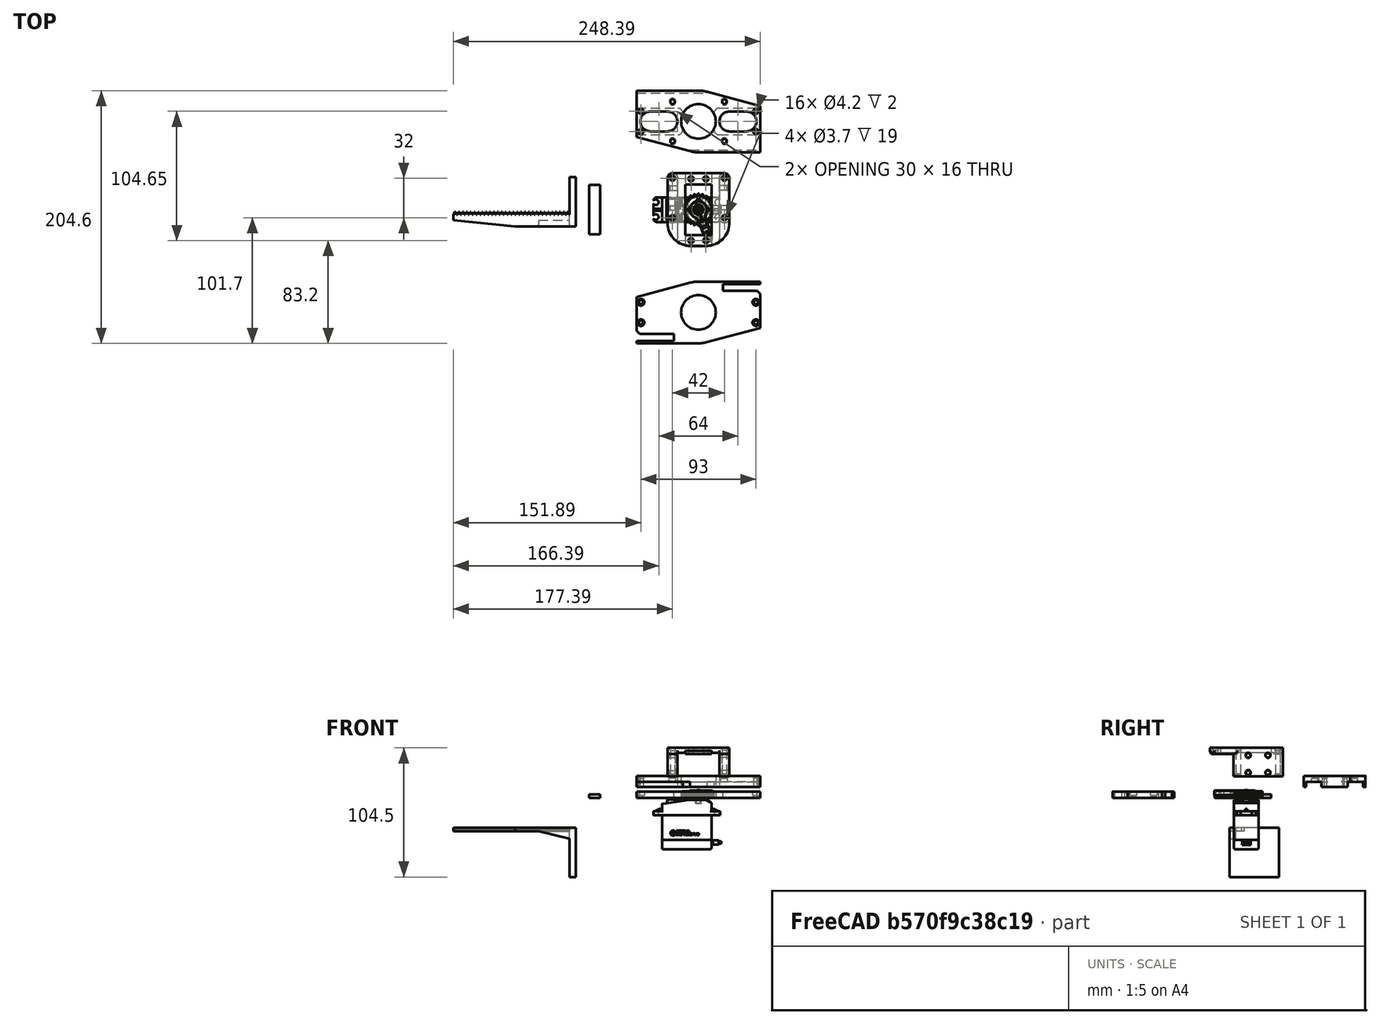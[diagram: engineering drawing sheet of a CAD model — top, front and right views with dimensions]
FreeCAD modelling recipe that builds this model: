
FCSTD DOCUMENT  (FreeCAD 1.1R20251125 (Git shallow))
Label: Pince_double_cremailleres
License: All rights reserved
LicenseURL: https://en.wikipedia.org/wiki/All_rights_reserved
objects: Sketcher::SketchObject×18, App::FeaturePython×13, PartDesign::Mirrored×11, App::Point×10, App::Link×9, PartDesign::Pad×7, PartDesign::Body×7, PartDesign::Pocket×6, PartDesign::Hole×6, PartDesign::Fillet×6, PartDesign::Chamfer×4, Part::FeaturePython×3, PartDesign::PolarPattern×3, PartDesign::MultiTransform×3, Part::Feature×3, PartDesign::FeatureBase×2, App::Part×2, PartDesign::Revolution×1, App::VarSet×1, Assembly::SimulationGroup×1, +2 more types
note: 177 computed .brp shape members not serialized (recipe doc carries the construction recipe); baked Part::Feature solids carry a one-line shape summary decoded from their .brp

FEATURE [Part::FeaturePython] InvoluteGear001  label="InvoluteGear_11_77"  # WARN: FeaturePython — macro-defined, semantics opaque (R4)
  AttacherType = Attacher::AttachEngine3D
  addendum_diameter = 26
  angular_backlash = 0
  axle_hole = false
  axle_holesize = 10
  backlash = 0
  clearance = 0.25
  double_helix = false
  head = 0
  head_fillet = 0
  height = 5.5
  helix_angle = 0
  module = 1
  num_teeth = 24
  numpoints = 20
  offset_hole = false
  offset_holeoffset = 10
  offset_holesize = 10
  pitch_diameter = 24
  pressure_angle = 20
  properties_from_tool = false
  reversed_backlash = false
  root_diameter = 21.5
  root_fillet = 0
  shift = 0
  simple = false
  transverse_pitch = 3.14159
  traverse_module = 1
  undercut = false
  version = 1.3.0
  expr: angular_backlash = backlash / pitch_diameter * 360 ° / pi
FEATURE [PartDesign::FeatureBase] BaseFeature003
  BaseFeature = -> InvoluteGear001
  Suppressed = false
FEATURE [Part::FeaturePython] InvoluteRack001  label="InvoluteRack_11_77"  # WARN: FeaturePython — macro-defined, semantics opaque (R4)
  AttacherType = Attacher::AttachEngine3D
  add_endings = true
  clearance = 0.25
  double_helix = false
  head = 0
  head_fillet = 0
  height = 3
  helix_angle = 0
  module = 1
  num_teeth = 30
  pressure_angle = 20
  properties_from_tool = false
  root_fillet = 0
  simplified = false
  thickness = 9.5
  transverse_pitch = 3.14159
  version = 1.3.0
FEATURE [PartDesign::FeatureBase] BaseFeature002
  BaseFeature = -> InvoluteRack001
  Suppressed = false
FEATURE [App::Point] Origin306  label="Origine"
  Role = Origin
FEATURE [App::Point] Origin311  label="Origine038"
  Role = Origin
FEATURE [App::Point] Origin312  label="Origine039"
  Role = Origin
FEATURE [App::Point] Origin314  label="Origine041"
  Role = Origin
FEATURE [Sketcher::SketchObject] Sketch244
  ArcFitTolerance = 1e-06
  AttachmentSupport = -> [BaseFeature002]
  ExternalTypes = [0]
  FullyConstrained = true
  MakeInternals = false
  MapMode = 5
  Placement = pos=(0,92.677,0) rot=(0,0.707107,0.707107;3.14159rad)
  sketch-geometry (4):
    g0: LineSegment StartX=-29.25 StartY=0 StartZ=0 EndX=10.75 EndY=0 EndZ=0
    g1: LineSegment StartX=10.75 StartY=0 StartZ=0 EndX=10.75 EndY=40 EndZ=0
    g2: LineSegment StartX=10.75 StartY=40 StartZ=0 EndX=-29.25 EndY=40 EndZ=0
    g3: LineSegment StartX=-29.25 StartY=40 StartZ=0 EndX=-29.25 EndY=0 EndZ=0
  constraints (12):
    c: Coincident(g0,g1)
    c: Coincident(g1,g2)
    c: Coincident(g2,g3)
    c: Coincident(g3,g0)
    c: Horizontal(g0)
    c: Horizontal(g2)
    c: Vertical(g1)
    c: Vertical(g3)
    c: DistanceY(g3,g3) = 40
    c: DistanceX(g2,g2) = 40
    c: PointOnObject(g0,g-1)
    c: DistanceX(g-1,g0) = 10.75
FEATURE [PartDesign::Pad] Pad119
  BaseFeature = -> BaseFeature002
  Direction = (0,1,-2e-16)
  Length = 5
  Length2 = 10
  Profile = -> Sketch244
  ReferenceAxis = -> Sketch244 [N_Axis]
  Refine = true
  SideType = 0
  Suppressed = false
  Type = 0
  Type2 = 0
FEATURE [Sketcher::SketchObject] Sketch253
  ArcFitTolerance = 0
  ExternalTypes = [0]
  FullyConstrained = true
  MakeInternals = false
  MapMode = 5
  Placement = pos=(0,0,5.5) rot=(0,0,1;0rad)
  sketch-geometry (8):
    g0: Circle [constr] CenterX=0 CenterY=0 CenterZ=0 NormalX=0 NormalY=0 NormalZ=1 AngleXU=0 Radius=7
    g1: Circle CenterX=0 CenterY=7 CenterZ=0 NormalX=0 NormalY=0 NormalZ=1 AngleXU=0 Radius=1.65
    g2: Circle CenterX=-7 CenterY=0 CenterZ=0 NormalX=0 NormalY=0 NormalZ=1 AngleXU=0 Radius=1.65
    g3: Circle CenterX=7 CenterY=0 CenterZ=0 NormalX=0 NormalY=0 NormalZ=1 AngleXU=0 Radius=1.65
    g4: Circle CenterX=0 CenterY=-7 CenterZ=0 NormalX=0 NormalY=0 NormalZ=1 AngleXU=0 Radius=1.65
    g5: Circle CenterX=0 CenterY=0 CenterZ=0 NormalX=0 NormalY=0 NormalZ=1 AngleXU=0 Radius=3
    g6: LineSegment [constr] StartX=-7 StartY=0 StartZ=0 EndX=7 EndY=0 EndZ=0
    g7: LineSegment [constr] StartX=0 StartY=7 StartZ=0 EndX=0 EndY=-7 EndZ=0
  constraints (20):
    c: Coincident(g5,g0)
    c: Coincident(g5,g-1)
    c: PointOnObject(g2,g0)
    c: PointOnObject(g1,g0)
    c: PointOnObject(g3,g0)
    c: PointOnObject(g4,g0)
    c: Coincident(g2,g6)
    c: Coincident(g1,g7)
    c: Coincident(g6,g3)
    c: Coincident(g7,g4)
    c: PointOnObject(g5,g7)
    c: PointOnObject(g5,g6)
    c: Perpendicular(g7,g6)
    c: Equal(g1,g3)
    c: Equal(g1,g2)
    c: Equal(g1,g4)
    c: Diameter(g1) = 3.3
    c: Diameter(g5) = 6
    c: Diameter(g0) = 14
    c: PointOnObject(g2,g-1)
FEATURE [PartDesign::Pocket] Pocket106
  BaseFeature = -> BaseFeature003
  Direction = (0,0,-1)
  Length = 5
  Length2 = 100
  Profile = -> Sketch253
  SideType = 0
  Suppressed = false
  Type = 1
  Type2 = 0
FEATURE [Sketcher::SketchObject] Sketch254
  ArcFitTolerance = 0
  AttachmentSupport = -> [Pocket106]
  ExternalGeometry = -> [Pocket106]
  ExternalTypes = [0]
  FullyConstrained = true
  MakeInternals = false
  MapMode = 5
  Placement = pos=(0,0,0) rot=(1,0,0;3.14159rad)
  sketch-geometry (4):
    g0: Circle CenterX=0 CenterY=-7 CenterZ=0 NormalX=0 NormalY=0 NormalZ=1 AngleXU=0 Radius=3.25
    g1: Circle CenterX=-7 CenterY=0 CenterZ=0 NormalX=0 NormalY=0 NormalZ=1 AngleXU=0 Radius=3.25
    g2: Circle CenterX=7 CenterY=0 CenterZ=0 NormalX=0 NormalY=0 NormalZ=1 AngleXU=0 Radius=3.25
    g3: Circle CenterX=0 CenterY=7 CenterZ=0 NormalX=0 NormalY=0 NormalZ=1 AngleXU=0 Radius=3.25
  constraints (8):
    c: Coincident(g1,g-5)
    c: Coincident(g0,g-3)
    c: Coincident(g2,g-4)
    c: Coincident(g3,g-6)
    c: Equal(g2,g0)
    c: Equal(g2,g1)
    c: Equal(g2,g3)
    c: Diameter(g2) = 6.5
FEATURE [PartDesign::Pocket] Pocket107
  BaseFeature = -> Pocket106
  Direction = (0,0,1)
  Length = 3.5
  Length2 = 100
  Profile = -> Sketch254
  SideType = 0
  Suppressed = false
  Type = 0
  Type2 = 0
FEATURE [PartDesign::Body] Body086  label="pignon"
  AllowCompound = false
  BaseFeature = -> InvoluteGear001
  Group = -> [BaseFeature003,Sketch253,Pocket106,Sketch254,Pocket107]
  Origin = -> Origin287
  Placement = pos=(-4.5e-15,0,0) rot=(0,0,1;0rad)
  Tip = -> Pocket107
FEATURE [Sketcher::SketchObject] Sketch259
  ArcFitTolerance = 1e-06
  AttachmentSupport = -> [XZ_Plane286]
  ExternalTypes = [0]
  FullyConstrained = true
  MakeInternals = false
  MapMode = 5
  Placement = pos=(0,0,0) rot=(1,0,0;1.5708rad)
  sketch-geometry (4):
    g0: LineSegment StartX=-4.5 StartY=0 StartZ=0 EndX=4.5 EndY=0 EndZ=0
    g1: LineSegment StartX=4.5 StartY=0 StartZ=0 EndX=4.5 EndY=3 EndZ=0
    g2: LineSegment StartX=4.5 StartY=3 StartZ=0 EndX=-4.5 EndY=3 EndZ=0
    g3: LineSegment StartX=-4.5 StartY=3 StartZ=0 EndX=-4.5 EndY=0 EndZ=0
  constraints (11):
    c: Coincident(g0,g1)
    c: Coincident(g1,g2)
    c: Coincident(g2,g3)
    c: Coincident(g3,g0)
    c: Horizontal(g0)
    c: Vertical(g1)
    c: Vertical(g3)
    c: PointOnObject(g0,g-1)
    c: Symmetric(g1,g2,g-2)
    c: Distance(g2,g2) = 9
    c: DistanceY(g3,g3) = 3
FEATURE [PartDesign::Pad] Pad123
  Direction = (0,-1,2e-16)
  Length = 40
  Length2 = 10
  Placement = pos=(0,0,0) rot=(1,0,0;1.5708rad)
  Profile = -> Sketch259
  ReferenceAxis = -> Sketch259 [N_Axis]
  SideType = 2
  Suppressed = false
  Type = 0
  Type2 = 0
FEATURE [PartDesign::Body] Body088  label="mousse"
  AllowCompound = false
  Group = -> [Sketch259,Pad123]
  Origin = -> Origin289
  Placement = pos=(-84,0,0) rot=(0,0,1;0rad)
  Tip = -> Pad123
FEATURE [Sketcher::SketchObject] Sketch262
  ArcFitTolerance = 1e-06
  AttachmentOffset = pos=(0,0,-10.75) rot=(0,0,1;0rad)
  AttachmentSupport = -> [YZ_Plane282]
  ExternalGeometry = -> [Pad119]
  ExternalTypes = [0]
  FullyConstrained = true
  MakeInternals = false
  MapMode = 5
  Placement = pos=(-10.75,0,0) rot=(0.57735,0.57735,0.57735;2.0944rad)
  sketch-geometry (3):
    g0: LineSegment StartX=67.677 StartY=3 StartZ=0 EndX=92.677 EndY=9 EndZ=0
    g1: LineSegment StartX=67.677 StartY=3 StartZ=0 EndX=92.677 EndY=3 EndZ=0
    g2: LineSegment StartX=92.677 StartY=9 StartZ=0 EndX=92.677 EndY=3 EndZ=0
  constraints (8):
    c: PointOnObject(g0,g-4)
    c: Coincident(g1,g0)
    c: Coincident(g1,g-4)
    c: Coincident(g2,g0)
    c: Coincident(g2,g1)
    c: DistanceX(g1,g1) = 25
    c: Vertical(g2)
    c: DistanceY(g2,g2) = 6
FEATURE [PartDesign::Pad] Pad124
  BaseFeature = -> Pad119
  Direction = (1,0,0)
  Length = 5
  Length2 = 10
  Profile = -> Sketch262
  ReferenceAxis = -> Sketch262 [N_Axis]
  SideType = 0
  Suppressed = false
  Type = 0
  Type2 = 0
FEATURE [App::Point] Origin317  label="Origine044"
  Role = Origin
FEATURE [Sketcher::SketchObject] Sketch
  ArcFitTolerance = 1e-06
  AttachmentSupport = -> [Origin]
  ExternalTypes = [0]
  FullyConstrained = true
  MakeInternals = false
  MapMode = 5
  expr: Constraints[23] = 28 / 2
  expr: Constraints[28] = 16.5 / 2
  sketch-geometry (17):
    g0: LineSegment StartX=-50 StartY=0 StartZ=0 EndX=-14 EndY=0 EndZ=0
    g1: LineSegment StartX=50 StartY=0 StartZ=0 EndX=50 EndY=15 EndZ=0
    g2: LineSegment [constr] StartX=1.5e-15 StartY=25 StartZ=0 EndX=-50 EndY=25 EndZ=0
    g3: LineSegment [constr] StartX=-50 StartY=25 StartZ=0 EndX=-50 EndY=12.5 EndZ=0
    g4: ArcOfCircle CenterX=0 CenterY=0 CenterZ=0 NormalX=0 NormalY=0 NormalZ=1 AngleXU=0 Radius=14 StartAngle=0 EndAngle=3.14159
    g5: LineSegment StartX=14 StartY=0 StartZ=0 EndX=50 EndY=0 EndZ=0
    g6: Circle CenterX=-46.5 CenterY=8.25 CenterZ=0 NormalX=0 NormalY=0 NormalZ=1 AngleXU=0 Radius=1.65
    g7: LineSegment StartX=50 StartY=23 StartZ=0 EndX=20 EndY=23 EndZ=0
    g8: LineSegment StartX=20 StartY=23 StartZ=0 EndX=20 EndY=17.5 EndZ=0
    g9: LineSegment StartX=20 StartY=17.5 StartZ=0 EndX=47.5 EndY=17.5 EndZ=0
    g10: LineSegment StartX=50 StartY=23 StartZ=0 EndX=50 EndY=25 EndZ=0
    g11: LineSegment StartX=47.5 StartY=17.5 StartZ=0 EndX=50 EndY=15 EndZ=0
    g12: Circle CenterX=46.5 CenterY=8.25 CenterZ=0 NormalX=0 NormalY=0 NormalZ=1 AngleXU=0 Radius=1.65
    g13: ArcOfCircle CenterX=0 CenterY=0 CenterZ=0 NormalX=0 NormalY=0 NormalZ=1 AngleXU=0 Radius=25 StartAngle=1.5708 EndAngle=1.83226
    g14: LineSegment StartX=-6.46242 StartY=24.1503 StartZ=0 EndX=-50 EndY=12.5 EndZ=0
    g15: LineSegment StartX=1.5e-15 StartY=25 StartZ=0 EndX=50 EndY=25 EndZ=0
    g16: LineSegment StartX=-50 StartY=12.5 StartZ=0 EndX=-50 EndY=0 EndZ=0
  constraints (47):
    c: Coincident(g5,g1)
    c: Coincident(g2,g3)
    c: PointOnObject(g0,g-1)
    c: Symmetric(g10,g2,g-2)
    c: Coincident(g4,g-1)
    c: Horizontal(g0)
    c: Horizontal(g5)
    c: Coincident(g4,g0)
    c: Coincident(g4,g5)
    c: Coincident(g7,g8)
    c: Coincident(g8,g9)
    c: Horizontal(g7)
    c: Vertical(g8)
    c: Vertical(g10)
    c: Coincident(g7,g10)
    c: Horizontal(g9)
    c: Coincident(g11,g9)
    c: Vertical(g1)
    c: Coincident(g11,g1)
    c: Vertical(g7,g1)
    c: Symmetric(g12,g6,g-2)
    c: Equal(g6,g12)
    c: DistanceX(g0,g6) = 3.5
    c: Radius(g4) = 14
    c: Angle(g11,g1) = 2.35619
    c: PointOnObject(g4,g-1)
    c: DistanceX(g7,g7) = 30
    c: DistanceY(g8,g8) = 5.5
    c: DistanceY(g1,g12) = 8.25
    c: DistanceY(g10,g10) = 2
    c: DistanceY(g1,g9) = 2.5
    c: Diameter(g12) = 3.3
    c: Coincident(g13,g4)
    c: Tangent(g14,g13) = -1.5708
    c: Coincident(g15,g13)
    c: Coincident(g16,g14)
    c: Coincident(g2,g13)
    c: DistanceX(g14,g10) = 100
    c: Coincident(g15,g10)
    c: Vertical(g3)
    c: Coincident(g3,g14)
    c: Coincident(g16,g0)
    c: DistanceY(g-1,g2) = 25
    c: Equal(g16,g3)
    c: Horizontal(g2)
    c: PointOnObject(g2,g-2)
    c: Vertical(g16)
FEATURE [PartDesign::Pad] Pad
  Direction = (0,0,1)
  Length = 5
  Length2 = 10
  Profile = -> Sketch
  ReferenceAxis = -> Sketch [N_Axis]
  SideType = 0
  Suppressed = false
  Type = 0
  Type2 = 0
FEATURE [PartDesign::Hole] Hole
  BaseFeature = -> Pad
  BaseProfileType = 7
  CustomThreadClearance = 0
  Depth = 3
  DepthType = 0
  Diameter = 5.5
  DrillForDepth = false
  DrillPoint = 0
  DrillPointAngle = 118
  HoleCutCountersinkAngle = 90
  HoleCutCustomValues = false
  HoleCutDepth = 0
  HoleCutDiameter = 0
  HoleCutType = 0
  ModelThread = false
  Profile = -> Pad [Edge45,Edge42]
  Suppressed = false
  Tapered = false
  TaperedAngle = 90
  ThreadClass = 0
  ThreadDepth = 3
  ThreadDepthType = 0
  ThreadDiameter = 5.5
  ThreadDirection = 0
  ThreadFit = 0
  ThreadSize = 0
  ThreadType = 0
  Threaded = false
  UseCustomThreadClearance = false
  expr: Depth = VarSet.h_tete_vis
  expr: Diameter = VarSet.d_tete_vis
FEATURE [PartDesign::PolarPattern] PolarPattern
  Angle = 360
  Axis = -> Sketch [N_Axis]
  BaseFeature = -> Hole
  Mode = 0
  Occurrences = 2
  Offset = 120
  Originals = -> [Pad,Hole]
  Refine = true
  SpacingPattern = [0]
  Spacings = [-1]
  Suppressed = false
  TransformMode = 0
FEATURE [PartDesign::Body] Body  label="capot"
  AllowCompound = false
  Group = -> [Sketch,Pad,Hole,PolarPattern]
  Origin = -> Origin
  Placement = pos=(0,-83.2,0) rot=(0,0,1;0rad)
  Tip = -> PolarPattern
FEATURE [App::Point] Origin319  label="Origine046"
  Role = Origin
FEATURE [Sketcher::SketchObject] Sketch263
  ArcFitTolerance = 0
  AttachmentOffset = pos=(0,0,-2) rot=(0,0,1;0rad)
  AttachmentSupport = -> [XY_Plane289]
  ExternalTypes = [0]
  FullyConstrained = true
  MakeInternals = false
  MapMode = 2
  Placement = pos=(0,0,-2) rot=(0,0,1;0rad)
  expr: Constraints[10] = 41 / 2
  expr: Constraints[13] = 59 / 2
  sketch-geometry (8):
    g0: LineSegment StartX=-10.5 StartY=20.5 StartZ=0 EndX=10.5 EndY=20.5 EndZ=0
    g1: LineSegment StartX=10.5 StartY=20.5 StartZ=0 EndX=10.5 EndY=0 EndZ=0
    g2: LineSegment StartX=-10.5 StartY=0 StartZ=0 EndX=-10.5 EndY=20.5 EndZ=0
    g3: LineSegment StartX=-25 StartY=29.5 StartZ=0 EndX=25 EndY=29.5 EndZ=0
    g4: LineSegment StartX=25 StartY=29.5 StartZ=0 EndX=25 EndY=0 EndZ=0
    g5: LineSegment StartX=25 StartY=0 StartZ=0 EndX=10.5 EndY=0 EndZ=0
    g6: LineSegment StartX=-25 StartY=0 StartZ=0 EndX=-25 EndY=29.5 EndZ=0
    g7: LineSegment StartX=-10.5 StartY=0 StartZ=0 EndX=-25 EndY=0 EndZ=0
  constraints (22):
    c: Coincident(g0,g1)
    c: Coincident(g2,g0)
    c: Horizontal(g0)
    c: Vertical(g1)
    c: Vertical(g2)
    c: Coincident(g3,g4)
    c: Coincident(g4,g5)
    c: Coincident(g6,g3)
    c: Vertical(g4)
    c: DistanceX(g2,g1) = 21
    c: DistanceY(g2,g2) = 20.5
    c: DistanceX(g7,g2) = 14.5
    c: Vertical(g6)
    c: DistanceY(g4,g4) = 29.5
    c: Coincident(g7,g6)
    c: Horizontal(g3)
    c: Symmetric(g1,g2,g-1)
    c: Symmetric(g4,g7,g-1)
    c: Horizontal(g5)
    c: Coincident(g5,g1)
    c: Coincident(g7,g2)
    c: PointOnObject(g2,g-1)
FEATURE [PartDesign::Pad] Pad125
  AlongSketchNormal = false
  Direction = (0,0,1)
  Length = 5
  Length2 = 100
  Profile = -> Sketch263
  ReferenceAxis = -> Sketch263 [N_Axis]
  SideType = 0
  Suppressed = false
  Type = 0
  Type2 = 0
FEATURE [PartDesign::Mirrored] Mirrored
  BaseFeature = -> Pad125
  MirrorPlane = -> Sketch263 [H_Axis]
  Originals = -> [Pad125]
  Refine = true
  Suppressed = false
  TransformMode = 0
FEATURE [Sketcher::SketchObject] Sketch271
  ArcFitTolerance = 1e-06
  AttachmentSupport = -> [Mirrored]
  ExternalGeometry = -> [Mirrored]
  ExternalTypes = [0]
  FullyConstrained = true
  MakeInternals = false
  MapMode = 5
  Placement = pos=(0,0,-2) rot=(1,0,0;3.14159rad)
  sketch-geometry (4):
    g0: LineSegment StartX=25 StartY=-29.5 StartZ=0 EndX=25 EndY=10.5 EndZ=0
    g1: LineSegment StartX=25 StartY=10.5 StartZ=0 EndX=17 EndY=10.5 EndZ=0
    g2: LineSegment StartX=17 StartY=10.5 StartZ=0 EndX=17 EndY=-29.5 EndZ=0
    g3: LineSegment StartX=17 StartY=-29.5 StartZ=0 EndX=25 EndY=-29.5 EndZ=0
  constraints (11):
    c: Coincident(g0,g1)
    c: Coincident(g1,g2)
    c: Coincident(g2,g3)
    c: Coincident(g3,g0)
    c: Vertical(g0)
    c: Vertical(g2)
    c: Horizontal(g1)
    c: Horizontal(g3)
    c: Distance(g0,g2) = 8
    c: Distance(g1,g3) = 40
    c: Coincident(g0,g-3)
FEATURE [PartDesign::Pad] Pad127
  BaseFeature = -> Mirrored
  Direction = (0,0,-1)
  Length = 18
  Length2 = 10
  Profile = -> Sketch271
  ReferenceAxis = -> Sketch271 [N_Axis]
  SideType = 0
  Suppressed = false
  Type = 0
  Type2 = 0
FEATURE [Sketcher::SketchObject] Sketch272
  ArcFitTolerance = 1e-06
  AttachmentSupport = -> [Pad127]
  ExternalGeometry = -> [Pad127]
  ExternalTypes = [0,0]
  FullyConstrained = true
  MakeInternals = false
  MapMode = 5
  Placement = pos=(0,0,3) rot=(0,0,1;0rad)
  sketch-geometry (6):
    g0: GeomPoint X=21 Y=25.5 Z=0
    g1: GeomPoint X=21 Y=-6.5 Z=0
    g2: LineSegment [constr] StartX=0 StartY=9.5 StartZ=0 EndX=25 EndY=9.5 EndZ=0
    g3: LineSegment [constr] StartX=21 StartY=29.5 StartZ=0 EndX=21 EndY=9.5 EndZ=0
    g4: GeomPoint X=6 Y=25 Z=0
    g5: GeomPoint X=6 Y=-25 Z=0
  constraints (12):
    c: PointOnObject(g2,g-2)
    c: Horizontal(g2)
    c: Symmetric(g-3,g-3,g2)
    c: Symmetric(g0,g1,g2)
    c: Symmetric(g-4,g-4,g3)
    c: PointOnObject(g3,g2)
    c: Vertical(g3)
    c: PointOnObject(g0,g3)
    c: DistanceY(g3,g0) = 16
    c: Distance(g4,g-2) = 6
    c: Symmetric(g4,g5,g-1)
    c: DistanceY(g-1,g4) = 25
FEATURE [PartDesign::Hole] Hole001
  BaseFeature = -> Pad127
  BaseProfileType = 1
  CustomThreadClearance = 0
  Depth = 26
  DepthType = 0
  Diameter = 3.7
  DrillForDepth = false
  DrillPoint = 0
  DrillPointAngle = 118
  HoleCutCountersinkAngle = 90
  HoleCutCustomValues = false
  HoleCutDepth = 2
  HoleCutDiameter = 4.2
  HoleCutType = 1
  ModelThread = false
  Profile = -> Sketch272
  Suppressed = false
  Tapered = false
  TaperedAngle = 90
  ThreadClass = 0
  ThreadDepth = 26
  ThreadDepthType = 0
  ThreadDiameter = 3.7
  ThreadDirection = 0
  ThreadFit = 0
  ThreadSize = 0
  ThreadType = 0
  Threaded = false
  UseCustomThreadClearance = false
  expr: Diameter = VarSet.d1_insert
  expr: HoleCutDepth = VarSet.h_d2_insert
  expr: HoleCutDiameter = VarSet.d2_insert
FEATURE [Sketcher::SketchObject] Sketch267
  ArcFitTolerance = 1e-06
  AttachmentSupport = -> [Hole001]
  ExternalGeometry = -> [Hole001]
  ExternalTypes = [0,0]
  FullyConstrained = true
  MakeInternals = false
  MapMode = 5
  Placement = pos=(25,0,0) rot=(0.57735,0.57735,0.57735;2.0944rad)
  sketch-geometry (6):
    g0: Circle CenterX=1.5 CenterY=-3 CenterZ=0 NormalX=0 NormalY=0 NormalZ=1 AngleXU=0 Radius=2.125
    g1: Circle CenterX=17.5 CenterY=-3 CenterZ=0 NormalX=0 NormalY=0 NormalZ=1 AngleXU=0 Radius=2.125
    g2: Circle CenterX=17.5 CenterY=-17 CenterZ=0 NormalX=0 NormalY=0 NormalZ=1 AngleXU=0 Radius=2.125
    g3: Circle CenterX=1.5 CenterY=-17 CenterZ=0 NormalX=0 NormalY=0 NormalZ=1 AngleXU=0 Radius=2.125
    g4: LineSegment [constr] StartX=9.5 StartY=-20 StartZ=0 EndX=9.5 EndY=0 EndZ=0
    g5: GeomPoint [constr] X=9.5 Y=-10 Z=0
  constraints (15):
    c: Equal(g0,g1)
    c: Equal(g1,g3)
    c: Equal(g3,g2)
    c: Diameter(g0) = 4.25
    c: Symmetric(g-3,g-3,g4)
    c: Vertical(g4)
    c: DistanceX(g0,g1) = 16
    c: DistanceY(g2,g1) = 14
    c: Vertical(g0,g3)
    c: Vertical(g2,g1)
    c: Horizontal(g1,g0)
    c: Horizontal(g2,g3)
    c: Symmetric(g4,g4,g5)
    c: Symmetric(g1,g3,g5)
    c: DistanceY(g-3,g3) = 3
FEATURE [PartDesign::Hole] Hole002
  BaseFeature = -> Hole001
  BaseProfileType = 7
  CustomThreadClearance = 0
  Depth = 25
  DepthType = 0
  Diameter = 3.7
  DrillForDepth = false
  DrillPoint = 0
  DrillPointAngle = 118
  HoleCutCountersinkAngle = 90
  HoleCutCustomValues = false
  HoleCutDepth = 2
  HoleCutDiameter = 4.2
  HoleCutType = 1
  ModelThread = false
  Profile = -> Sketch267
  Suppressed = false
  Tapered = false
  TaperedAngle = 90
  ThreadClass = 0
  ThreadDepth = 25
  ThreadDepthType = 0
  ThreadDiameter = 3.7
  ThreadDirection = 0
  ThreadFit = 0
  ThreadSize = 0
  ThreadType = 0
  Threaded = false
  UseCustomThreadClearance = false
  expr: Diameter = VarSet.d1_insert
  expr: HoleCutDepth = VarSet.h_d2_insert
  expr: HoleCutDiameter = VarSet.d2_insert
FEATURE [PartDesign::Mirrored] Mirrored001
  BaseFeature = -> Hole002
  MirrorPlane = -> Sketch271 [V_Axis]
  Originals = -> [Pad127,Hole001,Hole002]
  Suppressed = false
  TransformMode = 0
FEATURE [App::Point] Origin321  label="Origine047"
  Role = Origin
FEATURE [Sketcher::SketchObject] Sketch273
  ArcFitTolerance = 1e-06
  AttachmentSupport = -> [Origin320]
  ExternalTypes = [0]
  FullyConstrained = true
  MakeInternals = false
  MapMode = 5
  expr: Constraints[25] = 28 / 2
  sketch-geometry (9):
    g0: LineSegment StartX=14 StartY=1e-15 StartZ=0 EndX=17 EndY=1e-15 EndZ=0
    g1: LineSegment StartX=50 StartY=1e-15 StartZ=0 EndX=50 EndY=25 EndZ=0
    g2: LineSegment StartX=50 StartY=25 StartZ=0 EndX=0 EndY=25 EndZ=0
    g3: LineSegment StartX=9e-16 StartY=25 StartZ=0 EndX=9e-16 EndY=14 EndZ=0
    g4: ArcOfCircle CenterX=0 CenterY=0 CenterZ=0 NormalX=0 NormalY=0 NormalZ=1 AngleXU=0 Radius=14 StartAngle=0 EndAngle=1.5708
    g5: ArcOfCircle CenterX=25 CenterY=1e-15 CenterZ=0 NormalX=0 NormalY=0 NormalZ=1 AngleXU=0 Radius=8 StartAngle=1.5708 EndAngle=3.14159
    g6: ArcOfCircle CenterX=39 CenterY=3.1e-15 CenterZ=0 NormalX=0 NormalY=0 NormalZ=1 AngleXU=0 Radius=8 StartAngle=0 EndAngle=1.5708
    g7: LineSegment StartX=25 StartY=8 StartZ=0 EndX=39 EndY=8 EndZ=0
    g8: LineSegment StartX=47 StartY=1e-15 StartZ=0 EndX=50 EndY=1e-15 EndZ=0
  constraints (27):
    c: Coincident(g8,g1)
    c: Coincident(g1,g2)
    c: Coincident(g2,g3)
    c: Horizontal(g2)
    c: Vertical(g1)
    c: Coincident(g4,g0)
    c: Vertical(g3)
    c: Coincident(g4,g3)
    c: Tangent(g5,g7) = 1.5708
    c: Tangent(g6,g7) = 1.5708
    c: Equal(g5,g6)
    c: Horizontal(g7)
    c: Horizontal(g0)
    c: Horizontal(g8)
    c: Coincident(g6,g8)
    c: Coincident(g0,g5)
    c: Horizontal(g0,g6)
    c: PointOnObject(g0,g-1)
    c: Horizontal(g5,g0)
    c: Coincident(g4,g-1)
    c: PointOnObject(g3,g-2)
    c: DistanceX(g2,g2) = 50
    c: DistanceY(g1,g1) = 25
    c: Radius(g6) = 8
    c: DistanceX(g6,g1) = 11
    c: Radius(g4) = 14
    c: Equal(g8,g0)
FEATURE [PartDesign::Pad] Pad128
  Direction = (0,0,1)
  Length = 9
  Length2 = 10
  Profile = -> Sketch273
  ReferenceAxis = -> Sketch273 [N_Axis]
  SideType = 0
  Suppressed = false
  Type = 0
  Type2 = 0
FEATURE [PartDesign::Mirrored] Mirror
  MirrorPlane = -> XZ_Plane290
  Suppressed = false
  TransformMode = 0
FEATURE [PartDesign::Mirrored] Mirror001
  MirrorPlane = -> YZ_Plane290
  Suppressed = false
  TransformMode = 0
FEATURE [PartDesign::MultiTransform] MultiTransform
  BaseFeature = -> Pad128
  Refine = true
  Suppressed = false
  TransformMode = 1
  Transformations = -> [Mirror,Mirror001]
FEATURE [Sketcher::SketchObject] Sketch274
  ArcFitTolerance = 1e-06
  AttachmentSupport = -> [MultiTransform]
  ExternalGeometry = -> [MultiTransform]
  ExternalTypes = [0]
  FullyConstrained = true
  MakeInternals = false
  MapMode = 5
  Placement = pos=(-50,1.4e-14,0) rot=(0.57735,-0.57735,-0.57735;2.0944rad)
  sketch-geometry (4):
    g0: LineSegment StartX=-23 StartY=0 StartZ=0 EndX=-10.75 EndY=0 EndZ=0
    g1: LineSegment StartX=-10.75 StartY=0 StartZ=0 EndX=-10.75 EndY=4 EndZ=0
    g2: LineSegment StartX=-10.75 StartY=4 StartZ=0 EndX=-23 EndY=4 EndZ=0
    g3: LineSegment StartX=-23 StartY=4 StartZ=0 EndX=-23 EndY=0 EndZ=0
  constraints (12):
    c: Coincident(g0,g1)
    c: Coincident(g1,g2)
    c: Coincident(g2,g3)
    c: Coincident(g3,g0)
    c: Horizontal(g0)
    c: Horizontal(g2)
    c: Vertical(g1)
    c: Vertical(g3)
    c: Distance(g1,g3) = 12.25
    c: Distance(g0,g2) = 4
    c: PointOnObject(g0,g-1)
    c: DistanceX(g-3,g0) = 2
FEATURE [PartDesign::Pocket] Pocket
  BaseFeature = -> MultiTransform
  Direction = (1,0,0)
  Length = 5
  Length2 = 5
  Profile = -> Sketch274
  ReferenceAxis = -> Sketch274 [N_Axis]
  SideType = 0
  Suppressed = false
  Type = 1
  Type2 = 0
FEATURE [PartDesign::Mirrored] Mirrored002
  BaseFeature = -> Pocket
  MirrorPlane = -> Sketch274 [V_Axis]
  Originals = -> [Pocket]
  Suppressed = false
  TransformMode = 0
FEATURE [Sketcher::SketchObject] Sketch275
  ArcFitTolerance = 1e-06
  AttachmentSupport = -> [Mirrored002]
  ExternalTypes = [0]
  FullyConstrained = true
  MakeInternals = false
  MapMode = 5
  Placement = pos=(0,0,9) rot=(0,0,1;0rad)
  sketch-geometry (1):
    g0: GeomPoint X=46.5 Y=8.25 Z=0
  constraints (2):
    c: DistanceX(g-1,g0) = 46.5
    c: DistanceY(g-1,g0) = 8.25
FEATURE [PartDesign::Hole] Hole003
  BaseFeature = -> Mirrored002
  BaseProfileType = 7
  CustomThreadClearance = 0
  Depth = 25
  DepthType = 0
  Diameter = 3.7
  DrillForDepth = false
  DrillPoint = 0
  DrillPointAngle = 118
  HoleCutCountersinkAngle = 90
  HoleCutCustomValues = false
  HoleCutDepth = 2
  HoleCutDiameter = 4.2
  HoleCutType = 1
  ModelThread = false
  Profile = -> Sketch275
  Suppressed = false
  Tapered = false
  TaperedAngle = 90
  ThreadClass = 0
  ThreadDepth = 25
  ThreadDepthType = 0
  ThreadDiameter = 3.7
  ThreadDirection = 0
  ThreadFit = 0
  ThreadSize = 0
  ThreadType = 0
  Threaded = false
  UseCustomThreadClearance = false
  expr: Diameter = VarSet.d1_insert
  expr: HoleCutDepth = VarSet.h_d2_insert
  expr: HoleCutDiameter = VarSet.d2_insert
FEATURE [PartDesign::Mirrored] Mirror002
  MirrorPlane = -> Sketch275 [V_Axis]
  Suppressed = false
  TransformMode = 0
FEATURE [PartDesign::Mirrored] Mirror003
  MirrorPlane = -> Sketch275 [H_Axis]
  Suppressed = false
  TransformMode = 0
FEATURE [PartDesign::MultiTransform] MultiTransform001
  BaseFeature = -> Hole003
  Originals = -> [Hole003]
  Suppressed = false
  TransformMode = 0
  Transformations = -> [Mirror002,Mirror003]
FEATURE [Sketcher::SketchObject] Sketch276
  ArcFitTolerance = 1e-06
  AttachmentSupport = -> [MultiTransform001]
  ExternalTypes = [0]
  FullyConstrained = true
  MakeInternals = false
  MapMode = 5
  Placement = pos=(0,0,4) rot=(1,0,0;3.14159rad)
  expr: Constraints[0] = 32 / 2
  expr: Constraints[1] = 42 / 2
  sketch-geometry (1):
    g0: GeomPoint X=21 Y=16 Z=0
  constraints (2):
    c: DistanceY(g-1,g0) = 16
    c: DistanceX(g-1,g0) = 21
FEATURE [PartDesign::Hole] Hole004
  BaseFeature = -> MultiTransform001
  BaseProfileType = 7
  CustomThreadClearance = 0
  Depth = 10
  DepthType = 0
  Diameter = 3.7
  DrillForDepth = false
  DrillPoint = 0
  DrillPointAngle = 118
  HoleCutCountersinkAngle = 90
  HoleCutCustomValues = false
  HoleCutDepth = 3
  HoleCutDiameter = 5.5
  HoleCutType = 1
  ModelThread = false
  Profile = -> Sketch276
  Suppressed = false
  Tapered = false
  TaperedAngle = 90
  ThreadClass = 0
  ThreadDepth = 10
  ThreadDepthType = 0
  ThreadDiameter = 3.7
  ThreadDirection = 0
  ThreadFit = 0
  ThreadSize = 0
  ThreadType = 0
  Threaded = false
  UseCustomThreadClearance = false
  expr: Diameter = VarSet.d1_insert
  expr: HoleCutDepth = VarSet.h_tete_vis
  expr: HoleCutDiameter = VarSet.d_tete_vis
FEATURE [PartDesign::Mirrored] Mirror004
  MirrorPlane = -> Sketch276 [V_Axis]
  Suppressed = false
  TransformMode = 0
FEATURE [PartDesign::Mirrored] Mirror005
  MirrorPlane = -> Sketch276 [H_Axis]
  Suppressed = false
  TransformMode = 0
FEATURE [PartDesign::MultiTransform] MultiTransform002
  BaseFeature = -> Hole004
  Originals = -> [Hole004]
  Suppressed = false
  TransformMode = 0
  Transformations = -> [Mirror004,Mirror005]
FEATURE [PartDesign::Hole] Hole005
  BaseFeature = -> Mirrored001
  BaseProfileType = 7
  CustomThreadClearance = 0
  Depth = 2
  DepthType = 0
  Diameter = 4.2
  DrillForDepth = false
  DrillPoint = 0
  DrillPointAngle = 118
  HoleCutCountersinkAngle = 90
  HoleCutCustomValues = false
  HoleCutDepth = 0
  HoleCutDiameter = 0
  HoleCutType = 0
  ModelThread = false
  Profile = -> Mirrored001 [Edge143,Edge144]
  Reversed = true
  Suppressed = false
  Tapered = false
  TaperedAngle = 90
  ThreadClass = 0
  ThreadDepth = 2
  ThreadDepthType = 0
  ThreadDiameter = 4.2
  ThreadDirection = 0
  ThreadFit = 0
  ThreadSize = 0
  ThreadType = 0
  Threaded = false
  UseCustomThreadClearance = false
  expr: Depth = VarSet.h_d2_insert
  expr: Diameter = VarSet.d2_insert
FEATURE [PartDesign::Mirrored] Mirrored003
  BaseFeature = -> Hole005
  MirrorPlane = -> YZ_Plane289
  Originals = -> [Hole005]
  Suppressed = false
  TransformMode = 0
FEATURE [App::Point] Origin323  label="Origine049"
  Role = Origin
FEATURE [App::Link] cremaillere_bras  label="cremaillere_bras001"
  LinkPlacement = pos=(9.41322,21.75,-25) rot=(-0.707107,0.707107,0;3.14159rad)
  LinkedObject = -> Body084
  Placement = pos=(9.41322,21.75,-25) rot=(-0.707107,0.707107,0;3.14159rad)
FEATURE [App::Link] pignon  label="pignon001"
  LinkPlacement = pos=(8e-15,9.5,-26.2) rot=(0,0,-1;0.954906rad)
  LinkedObject = -> Body086
  Placement = pos=(8e-15,9.5,-26.2) rot=(0,0,-1;0.954906rad)
FEATURE [App::Link] mousse  label="mousse001"
  LinkPlacement = pos=(-83.2638,12.5,-60.5) rot=(0.707107,0,0.707107;3.14159rad)
  LinkedObject = -> Body088
  Placement = pos=(-83.2638,12.5,-60.5) rot=(0.707107,0,0.707107;3.14159rad)
FEATURE [App::Link] servo_DS3218MG003  label="servo_DS3218MG004"
  LinkPlacement = pos=(7.2e-15,9.5,-15.9) rot=(0.707107,0.707107,0;3.14159rad)
  LinkedObject = -> Part [Part002005.]
  Placement = pos=(7.2e-15,9.5,-15.9) rot=(0.707107,0.707107,0;3.14159rad)
FEATURE [App::Link] capot  label="capot001"
  LinkPlacement = pos=(-3.4e-15,9.5,-29) rot=(0,1,0;3.14159rad)
  LinkedObject = -> Body
  Placement = pos=(-3.4e-15,9.5,-29) rot=(0,1,0;3.14159rad)
FEATURE [App::Link] support_servo  label="support_servo001"
  LinkedObject = -> Body089
FEATURE [App::Link] support_cremaillere  label="support_cremaillere001"
  LinkPlacement = pos=(6e-15,9.5,-29) rot=(0,0,1;3.14159rad)
  LinkedObject = -> Body090
  Placement = pos=(6e-15,9.5,-29) rot=(0,0,1;3.14159rad)
FEATURE [App::Link] cremaillere_bras001  label="cremaillere_bras002"
  LinkPlacement = pos=(-9.43366,-2.75,-25) rot=(0.707107,0.707107,0;3.14159rad)
  LinkedObject = -> Body084
  Placement = pos=(-9.43366,-2.75,-25) rot=(0.707107,0.707107,0;3.14159rad)
FEATURE [App::Link] mousse001  label="mousse002"
  LinkPlacement = pos=(80.2433,6.5,-60.5) rot=(0,1,0;1.5708rad)
  LinkedObject = -> Body088
  Placement = pos=(80.2433,6.5,-60.5) rot=(0,1,0;1.5708rad)
FEATURE [App::FeaturePython] GroundedJoint  label="GroundedJoint002"  # Assembly grounded joint (typed FeaturePython)
  ObjectToGround = -> support_servo
FEATURE [App::Point] Origin326  label="Origine051"
  Role = Origin
FEATURE [App::Point] Origin327  label="Origine052"
  Role = Origin
FEATURE [Part::Feature] Part__Feature006  label="Lever 25T003"
  Placement = pos=(0,0,0) rot=(-1,0,0;1.5708rad)
  shape: bbox 18.84 x 33.03 x 6.019 mm, 125 faces (baked)
FEATURE [Part::Feature] Part__Feature007  label="Axis Servo003"
  Placement = pos=(0,0,0) rot=(-1,0,0;1.5708rad)
  shape: bbox 5 x 5 x 8 mm, 5 faces (baked)
FEATURE [Part::Feature] Part__Feature008  label="Servo DS3218MG003"
  Placement = pos=(0,0,0) rot=(-1,0,0;1.5708rad)
  shape: bbox 55 x 20 x 41 mm, 772 faces (baked)
FEATURE [Part::FeaturePython] Screw006  label="M2x5-Vis003"  # WARN: FeaturePython — macro-defined, semantics opaque (R4)
  BaseObject = -> Body091 [Edge6]
  Diameter = 2
  Invert = true
  LeftHanded = false
  Length = 10
  LengthCustom = 5
  MatchOuter = false
  OffsetAngle = 0
  Placement = pos=(0,1e-15,4.8) rot=(0,0,1;0rad)
  Thread = false
  Type = 76
FEATURE [Sketcher::SketchObject] Sketch277
  ArcFitTolerance = 0
  AttachmentSupport = -> [XZ_Plane293]
  ExternalTypes = [0]
  FullyConstrained = true
  MakeInternals = false
  MapMode = 5
  Placement = pos=(0,0,0) rot=(1,0,0;1.5708rad)
  expr: Constraints[19] = 19.8 / 2
  sketch-geometry (8):
    g0: LineSegment StartX=2.5 StartY=3.4 StartZ=0 EndX=2.5 EndY=0 EndZ=0
    g1: LineSegment StartX=2.5 StartY=0 StartZ=0 EndX=4.2 EndY=0 EndZ=0
    g2: LineSegment StartX=4.2 StartY=0 StartZ=0 EndX=4.2 EndY=2 EndZ=0
    g3: LineSegment StartX=4.2 StartY=2 StartZ=0 EndX=9.9 EndY=2 EndZ=0
    g4: LineSegment StartX=9.9 StartY=2 StartZ=0 EndX=9.9 EndY=4.4 EndZ=0
    g5: LineSegment StartX=9.9 StartY=4.4 StartZ=0 EndX=1.5 EndY=4.4 EndZ=0
    g6: LineSegment StartX=1.5 StartY=4.4 StartZ=0 EndX=1.5 EndY=3.4 EndZ=0
    g7: LineSegment StartX=1.5 StartY=3.4 StartZ=0 EndX=2.5 EndY=3.4 EndZ=0
  constraints (24):
    c: PointOnObject(g0,g-1)
    c: Vertical(g0)
    c: Coincident(g1,g0)
    c: PointOnObject(g1,g-1)
    c: Coincident(g2,g1)
    c: Vertical(g2)
    c: Coincident(g3,g2)
    c: Horizontal(g3)
    c: Coincident(g4,g3)
    c: Vertical(g4)
    c: Coincident(g5,g4)
    c: Horizontal(g5)
    c: Coincident(g6,g5)
    c: Coincident(g7,g6)
    c: Coincident(g7,g0)
    c: Horizontal(g7)
    c: Vertical(g6)
    c: DistanceY(g4,g4) = 2.4
    c: DistanceY(g2,g2) = 2
    c: DistanceX(g-1,g4) = 9.9
    c: DistanceX(g-1,g6) = 1.5
    c: DistanceY(g0,g0) = 3.4
    c: DistanceX(g-1,g0) = 2.5
    c: DistanceX(g1,g1) = 1.7
FEATURE [PartDesign::Revolution] Revolution003
  Angle = 360
  Angle2 = 60
  Axis = (0,2e-16,1)
  Base = (0,0,0)
  Placement = pos=(0,0,0) rot=(1,0,0;1.5708rad)
  Profile = -> Sketch277
  ReferenceAxis = -> Sketch277 [V_Axis]
  Reversed = true
  Suppressed = false
  Type = 0
FEATURE [Sketcher::SketchObject] Sketch278
  ArcFitTolerance = 0
  AttachmentSupport = -> [XY_Plane293]
  ExternalTypes = [0]
  FullyConstrained = true
  MakeInternals = false
  MapMode = 5
  sketch-geometry (1):
    g0: Circle CenterX=-7 CenterY=0 CenterZ=0 NormalX=0 NormalY=0 NormalZ=1 AngleXU=0 Radius=1.2
  constraints (3):
    c: PointOnObject(g0,g-1)
    c: Diameter(g0) = 2.4
    c: DistanceX(g0,g-1) = 7
FEATURE [PartDesign::Pocket] Pocket112
  BaseFeature = -> Revolution003
  Direction = (0,0,-1)
  Length = 5
  Length2 = 5
  Placement = pos=(0,0,0) rot=(1,0,0;1.5708rad)
  Profile = -> Sketch278
  ReferenceAxis = -> Sketch278 [N_Axis]
  SideType = 2
  Suppressed = false
  Type = 1
  Type2 = 0
FEATURE [PartDesign::PolarPattern] PolarPattern007
  Angle = 360
  Axis = -> Sketch278 [N_Axis]
  BaseFeature = -> Pocket112
  Mode = 0
  Occurrences = 4
  Offset = 120
  Originals = -> [Pocket112]
  Placement = pos=(0,0,0) rot=(1,0,0;1.5708rad)
  SpacingPattern = [0]
  Spacings = [-1,-1,-1]
  Suppressed = false
  TransformMode = 0
FEATURE [PartDesign::Body] Body091  label="Corps003"
  AllowCompound = false
  Group = -> [Sketch277,Revolution003,Sketch278,Pocket112,PolarPattern007]
  Origin = -> Origin325
  Placement = pos=(0,0,0.4) rot=(0,0,1;0rad)
  Tip = -> PolarPattern007
FEATURE [App::Part] Part002005  label="servo_DS3218MG005"
  Group = -> [Part__Feature006,Part__Feature007,Part__Feature008,Body091,Screw006]
  Origin = -> Origin324
FEATURE [App::FeaturePython] Joint010  label="Revolute016"  # Assembly joint (typed FeaturePython)
  Angle = 0
  AngleMax = 0
  AngleMin = 0
  Detach1 = false
  Detach2 = false
  Distance = 0
  Distance2 = 0
  EnableAngleMax = false
  EnableAngleMin = false
  EnableLengthMax = false
  EnableLengthMin = false
  JointType = 1 (Revolute)
  LengthMax = 0
  LengthMin = 0
  Placement1 = pos=(0,0,5.5) rot=(0,0,1;0rad)
  Reference1 = -> Assembly002 [pignon.Edge300,pignon.Edge300]
  Reference2 = -> Assembly002 [servo_DS3218MG003.Screw006.Edge63,servo_DS3218MG003.Screw006.Edge63]
  Suppressed = false
FEATURE [App::VarSet] VarSet
  d1_insert = 3.7
  d2_insert = 4.2
  d_tete_vis = 5.5
  h_d2_insert = 2
  h_tete_vis = 3
FEATURE [PartDesign::Fillet] Fillet
  Base = -> Mirrored003 [Edge67,Edge54]
  BaseFeature = -> Mirrored003
  Radius = 4
  SupportTransform = false
  Suppressed = false
  UseAllEdges = false
FEATURE [PartDesign::Fillet] Fillet001
  Base = -> Fillet [Edge3,Edge29]
  BaseFeature = -> Fillet
  Radius = 19
  SupportTransform = false
  Suppressed = false
  UseAllEdges = false
FEATURE [App::FeaturePython] Joint013  label="Fixed019"  # Assembly joint (typed FeaturePython)
  Angle = 0
  AngleMax = 0
  AngleMin = 0
  Detach1 = false
  Detach2 = false
  Distance = 0
  Distance2 = 0
  EnableAngleMax = false
  EnableAngleMin = false
  EnableLengthMax = false
  EnableLengthMin = false
  JointType = 0 (Fixed)
  LengthMax = 0
  LengthMin = 0
  Offset2 = pos=(0,0,0) rot=(0,0,1;3.14159rad)
  Placement1 = pos=(15.5,13.9,-6) rot=(0.57735,0.57735,0.57735;4.18879rad)
  Placement2 = pos=(-6,25,-2) rot=(1,0,0;3.14159rad)
  Reference1 = -> Assembly002 [servo_DS3218MG003.Part__Feature008.Edge1093,servo_DS3218MG003.Part__Feature008.Edge1093]
  Reference2 = -> Assembly002 [support_servo.Edge188,support_servo.Edge188]
  Suppressed = false
FEATURE [Sketcher::SketchObject] Sketch279
  ArcFitTolerance = 1e-06
  AttachmentSupport = -> [MultiTransform002]
  ExternalGeometry = -> [MultiTransform002]
  ExternalTypes = [0,0]
  FullyConstrained = true
  MakeInternals = false
  MapMode = 5
  Placement = pos=(0,0,4) rot=(1,0,0;3.14159rad)
  sketch-geometry (5):
    g0: LineSegment StartX=-50 StartY=12.5 StartZ=0 EndX=-6.46242 EndY=24.1503 EndZ=0
    g1: LineSegment StartX=1.5e-15 StartY=25 StartZ=0 EndX=-50 EndY=25 EndZ=0
    g2: LineSegment StartX=-50 StartY=25 StartZ=0 EndX=-50 EndY=12.5 EndZ=0
    g3: ArcOfCircle CenterX=0 CenterY=0 CenterZ=0 NormalX=0 NormalY=0 NormalZ=1 AngleXU=0 Radius=25 StartAngle=1.5708 EndAngle=1.83226
    g4: LineSegment [constr] StartX=-50 StartY=-1.21e-14 StartZ=0 EndX=-50 EndY=25 EndZ=0
  constraints (11):
    c: Horizontal(g1)
    c: Coincident(g2,g1)
    c: Coincident(g2,g0)
    c: Coincident(g3,g-1)
    c: Coincident(g3,g1)
    c: Tangent(g0,g3) = 1.5708
    c: Coincident(g1,g-4)
    c: Symmetric(g-3,g-3,g4)
    c: Coincident(g4,g1)
    c: Symmetric(g1,g4,g0)
    c: PointOnObject(g1,g-2)
FEATURE [PartDesign::Pocket] Pocket113
  BaseFeature = -> MultiTransform002
  Direction = (0,0,1)
  Length = 5
  Length2 = 5
  Profile = -> Sketch279
  ReferenceAxis = -> Sketch279 [N_Axis]
  SideType = 2
  Suppressed = false
  Type = 1
  Type2 = 0
FEATURE [PartDesign::PolarPattern] PolarPattern008
  Angle = 360
  Axis = -> Sketch279 [N_Axis]
  BaseFeature = -> Pocket113
  Mode = 0
  Occurrences = 2
  Offset = 120
  Originals = -> [Pocket113]
  SpacingPattern = [0]
  Spacings = [-1]
  Suppressed = false
  TransformMode = 0
FEATURE [PartDesign::Chamfer] Chamfer001
  Angle = 45
  Base = -> PolarPattern008 [Edge18,Edge133]
  BaseFeature = -> PolarPattern008
  ChamferType = 0
  FlipDirection = false
  Size = 4
  Size2 = 1
  SupportTransform = false
  Suppressed = false
  UseAllEdges = false
FEATURE [PartDesign::Fillet] Fillet004
  Base = -> Chamfer001 [Edge94,Edge89,Edge76,Edge95]
  BaseFeature = -> Chamfer001
  Radius = 4
  SupportTransform = false
  Suppressed = false
  UseAllEdges = false
FEATURE [PartDesign::Body] Body090  label="support_cremaillere"
  AllowCompound = false
  Group = -> [Sketch273,Pad128,MultiTransform,Mirror,Mirror001,Sketch274,Pocket,Mirrored002,Sketch275,Hole003,MultiTransform001,Mirror002,Mirror003,Sketch276,Hole004,MultiTransform002,Mirror004,Mirror005,Sketch279,Pocket113,PolarPattern008,Chamfer001,Fillet004]
  Origin = -> Origin320
  Placement = pos=(8.5e-15,71.4,8.9) rot=(0,0,1;0rad)
  Tip = -> Fillet004
FEATURE [PartDesign::Chamfer] Chamfer002
  Angle = 45
  Base = -> Pad124 [Edge2]
  BaseFeature = -> Pad124
  ChamferType = 1
  FlipDirection = false
  Size = 5
  Size2 = 50
  SupportTransform = false
  Suppressed = false
  UseAllEdges = false
FEATURE [PartDesign::Body] Body084  label="cremaillere_bras"
  AllowCompound = false
  BaseFeature = -> InvoluteRack001
  Group = -> [BaseFeature002,Sketch244,Pad119,Sketch262,Pad124,Chamfer002]
  Origin = -> Origin285
  Placement = pos=(-196.823,-2.75,-24) rot=(0.707107,0.707107,0;3.14159rad)
  Tip = -> Chamfer002
FEATURE [App::FeaturePython] Joint014  label="Slider025"  # Assembly joint (typed FeaturePython)
  Angle = 0
  AngleMax = 0
  AngleMin = 0
  Detach1 = false
  Detach2 = false
  Distance = 0
  Distance2 = 0
  EnableAngleMax = false
  EnableAngleMin = false
  EnableLengthMax = true
  EnableLengthMin = true
  JointType = 3 (Slider)
  LengthMax = -9
  LengthMin = -42
  Offset2 = pos=(0,0,0) rot=(0,0,1;3.14159rad)
  Placement1 = pos=(-10.75,73.0531,3.6e-15) rot=(0.57735,0.57735,0.57735;4.18879rad)
  Placement2 = pos=(-21.6194,23,4) rot=(0,-1,0;4.71239rad)
  Reference1 = -> Assembly002 [cremaillere_bras001.Edge7,cremaillere_bras001.Edge7]
  Reference2 = -> Assembly002 [support_cremaillere.Edge5,support_cremaillere.Edge5]
  Suppressed = false
FEATURE [App::FeaturePython] Joint015  label="Slider026"  # Assembly joint (typed FeaturePython)
  Angle = 0
  AngleMax = 0
  AngleMin = 0
  Detach1 = false
  Detach2 = false
  Distance = 0
  Distance2 = 0
  EnableAngleMax = false
  EnableAngleMin = false
  EnableLengthMax = false
  EnableLengthMin = false
  JointType = 3 (Slider)
  LengthMax = -9
  LengthMin = -42
  Offset2 = pos=(0,0,0) rot=(0,0,1;3.14159rad)
  Placement1 = pos=(-10.75,73.0531,7.1e-15) rot=(0.57735,0.57735,0.57735;4.18879rad)
  Placement2 = pos=(21.6194,-23,4) rot=(0,-1,0;4.71239rad)
  Reference1 = -> Assembly002 [cremaillere_bras.Edge7,cremaillere_bras.Edge7]
  Reference2 = -> Assembly002 [support_cremaillere.Edge112,support_cremaillere.Edge112]
  Suppressed = false
FEATURE [App::FeaturePython] Joint016  label="Fixed023"  # Assembly joint (typed FeaturePython)
  Angle = 0
  AngleMax = 0
  AngleMin = 0
  Detach1 = false
  Detach2 = false
  Distance = 0
  Distance2 = 0
  EnableAngleMax = false
  EnableAngleMin = false
  EnableLengthMax = false
  EnableLengthMin = false
  JointType = 0 (Fixed)
  LengthMax = 0
  LengthMin = 0
  Placement1 = pos=(-46.5,-8.25,0) rot=(0,0,1;3.14159rad)
  Placement2 = pos=(-46.5,8.25,-7.1e-15) rot=(0,-1,0;3.14159rad)
  Reference1 = -> Assembly002 [capot.Edge41,capot.Edge41]
  Reference2 = -> Assembly002 [support_cremaillere.Edge78,support_cremaillere.Edge78]
  Suppressed = false
FEATURE [App::FeaturePython] Joint017  label="Fixed024"  # Assembly joint (typed FeaturePython)
  Angle = 0
  AngleMax = 0
  AngleMin = 0
  Detach1 = false
  Detach2 = false
  Distance = 0
  Distance2 = 0
  EnableAngleMax = false
  EnableAngleMin = false
  EnableLengthMax = false
  EnableLengthMin = false
  JointType = 0 (Fixed)
  LengthMax = 0
  LengthMin = 0
  Offset2 = pos=(0,0,0) rot=(0,0,1;1.5708rad)
  Placement1 = pos=(4.5,2.7e-15,3) rot=(-0.57735,-0.57735,0.57735;4.18879rad)
  Placement2 = pos=(9.25,92.677,40) rot=(0.57735,-0.57735,0.57735;4.18879rad)
  Reference1 = -> Assembly002 [mousse001.Edge5,mousse001.Edge5]
  Reference2 = -> Assembly002 [cremaillere_bras001.Edge271,cremaillere_bras001.Edge271]
  Suppressed = false
FEATURE [App::FeaturePython] Joint018  label="Fixed025"  # Assembly joint (typed FeaturePython)
  Angle = 0
  AngleMax = 0
  AngleMin = 0
  Detach1 = false
  Detach2 = false
  Distance = 0
  Distance2 = 0
  EnableAngleMax = false
  EnableAngleMin = false
  EnableLengthMax = false
  EnableLengthMin = false
  JointType = 0 (Fixed)
  LengthMax = 0
  LengthMin = 0
  Offset2 = pos=(0,0,0) rot=(0,0,-1;1.5708rad)
  Placement1 = pos=(-4.5,-1.8e-15,0) rot=(-0.57735,-0.57735,0.57735;4.18879rad)
  Placement2 = pos=(9.25,92.677,40) rot=(0.57735,0.57735,0.57735;2.0944rad)
  Reference1 = -> Assembly002 [mousse.Edge1,mousse.Edge1]
  Reference2 = -> Assembly002 [cremaillere_bras.Edge271,cremaillere_bras.Edge271]
  Suppressed = false
FEATURE [App::FeaturePython] Joint019  label="RackPinion031"  # Assembly joint (typed FeaturePython)
  Angle = 0
  AngleMax = 0
  AngleMin = 0
  Detach1 = false
  Detach2 = false
  Distance = 12
  Distance2 = 0
  EnableAngleMax = false
  EnableAngleMin = false
  EnableLengthMax = false
  EnableLengthMin = false
  JointType = 9 (RackPinion)
  LengthMax = 0
  LengthMin = 0
  Placement1 = pos=(-10.75,58.0531,3) rot=(0.57735,0.57735,0.57735;4.18879rad)
  Reference1 = -> Assembly002 [cremaillere_bras001.Edge135,cremaillere_bras001.Edge135]
  Reference2 = -> Assembly002 [pignon.Edge154,pignon.Edge154]
  Suppressed = false
FEATURE [App::FeaturePython] Joint020  label="RackPinion032"  # Assembly joint (typed FeaturePython)
  Angle = 0
  AngleMax = 0
  AngleMin = 0
  Detach1 = false
  Detach2 = false
  Distance = 12
  Distance2 = 0
  EnableAngleMax = false
  EnableAngleMin = false
  EnableLengthMax = false
  EnableLengthMin = false
  JointType = 9 (RackPinion)
  LengthMax = 0
  LengthMin = 0
  Placement1 = pos=(-10.75,58.0531,3) rot=(0.57735,0.57735,0.57735;4.18879rad)
  Reference1 = -> Assembly002 [cremaillere_bras.Edge135,cremaillere_bras.Edge135]
  Reference2 = -> Assembly002 [pignon.Edge154,pignon.Edge154]
  Suppressed = false
FEATURE [App::FeaturePython] Motion  label="Slider025 (Linear)"  # WARN: FeaturePython — macro-defined, semantics opaque (R4)
  Formula = -9-25*time
  Joint = -> Joint014
  MotionType = 1
FEATURE [App::FeaturePython] Simulation  label="Simulation002"  # WARN: FeaturePython — macro-defined, semantics opaque (R4)
  Group = -> [Motion]
  aTimeStart = 0
  bTimeEnd = 1
  cTimeStepOutput = 0.01
  fGlobalErrorTolerance = 1e-06
  jFramesPerSecond = 30
FEATURE [Assembly::SimulationGroup] Simulations
  Group = -> [Simulation]
FEATURE [Sketcher::SketchObject] Sketch281
  ArcFitTolerance = 1e-06
  AttachmentSupport = -> [Fillet001]
  ExternalGeometry = -> [Fillet001]
  ExternalTypes = [0,0]
  FullyConstrained = true
  MakeInternals = false
  MapMode = 5
  Placement = pos=(0,29.5,0) rot=(0,0.707107,0.707107;3.14159rad)
  sketch-geometry (4):
    g0: LineSegment StartX=-17 StartY=-2 StartZ=0 EndX=-10.5 EndY=-2 EndZ=0
    g1: LineSegment StartX=-10.5 StartY=-2 StartZ=0 EndX=-10.5 EndY=-1 EndZ=0
    g2: LineSegment StartX=-10.5 StartY=-1 StartZ=0 EndX=-17 EndY=-1 EndZ=0
    g3: LineSegment StartX=-17 StartY=-1 StartZ=0 EndX=-17 EndY=-2 EndZ=0
  constraints (11):
    c: Coincident(g0,g1)
    c: Coincident(g1,g2)
    c: Coincident(g2,g3)
    c: Coincident(g3,g0)
    c: Horizontal(g0)
    c: Horizontal(g2)
    c: Vertical(g1)
    c: Vertical(g3)
    c: Coincident(g0,g-3)
    c: Vertical(g1,g-4)
    c: DistanceY(g1,g1) = 1
FEATURE [PartDesign::Pocket] Pocket114
  BaseFeature = -> Fillet001
  Direction = (0,-1,2e-16)
  Length = 5
  Length2 = 5
  Profile = -> Sketch281
  ReferenceAxis = -> Sketch281 [N_Axis]
  SideType = 0
  Suppressed = false
  Type = 1
  Type2 = 0
FEATURE [PartDesign::Mirrored] Mirrored004
  BaseFeature = -> Pocket114
  MirrorPlane = -> Sketch281 [V_Axis]
  Originals = -> [Pocket114]
  Suppressed = false
  TransformMode = 0
FEATURE [PartDesign::Fillet] Fillet002
  Base = -> Mirrored004 [Edge40,Edge193,Edge153,Edge123]
  BaseFeature = -> Mirrored004
  Radius = 3.5
  SupportTransform = false
  Suppressed = false
  UseAllEdges = false
FEATURE [PartDesign::Chamfer] Chamfer
  Angle = 45
  Base = -> Fillet002 [Edge71,Edge174]
  BaseFeature = -> Fillet002
  ChamferType = 0
  FlipDirection = false
  Size = 2
  Size2 = 1
  SupportTransform = false
  Suppressed = false
  UseAllEdges = false
FEATURE [PartDesign::Fillet] Fillet005
  Base = -> Chamfer [Edge132,Edge94]
  BaseFeature = -> Chamfer
  Radius = 2
  SupportTransform = false
  Suppressed = false
  UseAllEdges = false
FEATURE [PartDesign::Chamfer] Chamfer003
  Angle = 45
  Base = -> Fillet005 [Edge92]
  BaseFeature = -> Fillet005
  ChamferType = 1
  FlipDirection = false
  Size = 1
  Size2 = 2.5
  SupportTransform = false
  Suppressed = false
  UseAllEdges = false
FEATURE [PartDesign::Fillet] Fillet006
  Base = -> Chamfer003 [Edge9,Edge80]
  BaseFeature = -> Chamfer003
  Radius = 2
  SupportTransform = false
  Suppressed = false
  UseAllEdges = false
FEATURE [PartDesign::Body] Body089  label="support_servo"
  AllowCompound = false
  Group = -> [Sketch263,Pad125,Mirrored,Sketch271,Pad127,Sketch272,Hole001,Sketch267,Hole002,Mirrored001,Hole005,Mirrored003,Fillet,Fillet001,Sketch281,Pocket114,Mirrored004,Fillet002,Chamfer,Fillet005,Chamfer003,Fillet006]
  Origin = -> Origin318
  Placement = pos=(0,0,37.5) rot=(0,0,1;0rad)
  Tip = -> Fillet006
FEATURE [App::Part] Part  label="Pince"
  Group = -> [InvoluteRack001,Body084,InvoluteGear001,Body086,Body088,Body,Body089,Body090,Part002005]
  Origin = -> Origin322
  Placement = pos=(-129.5,0,0) rot=(0,0,1;0rad)
FEATURE [App::FeaturePython] Joint  label="Fixed"  # Assembly joint (typed FeaturePython)
  Angle = 0
  AngleMax = 0
  AngleMin = 0
  Detach1 = false
  Detach2 = false
  Distance = 0
  Distance2 = 0
  EnableAngleMax = false
  EnableAngleMin = false
  EnableLengthMax = false
  EnableLengthMin = false
  JointType = 0 (Fixed)
  LengthMax = 0
  LengthMin = 0
  Offset2 = pos=(0,0,0) rot=(0,0,1;3.14159rad)
  Placement1 = pos=(-21,-16,9) rot=(0,0,1;0rad)
  Placement2 = pos=(21,25.5,-20) rot=(0,0,1;3.14159rad)
  Reference1 = -> Assembly002 [support_cremaillere.Edge87,support_cremaillere.Edge87]
  Reference2 = -> Assembly002 [support_servo.Edge240,support_servo.Edge240]
  Suppressed = false
FEATURE [Assembly::JointGroup] Joints002
  Group = -> [GroundedJoint,Joint010,Joint013,Joint014,Joint015,Joint016,Joint017,Joint018,Joint019,Joint020,Joint]
FEATURE [Assembly::AssemblyObject] Assembly002  label="Assembly_pince"
  Group = -> [Joints002,cremaillere_bras,pignon,mousse,servo_DS3218MG003,capot,support_servo,support_cremaillere,cremaillere_bras001,mousse001,GroundedJoint,Joint010,Joint013,Joint014,Joint015,Joint016,Joint017,Joint018,Joint019,Joint020,Simulations,Simulation,Motion,Joint]
  Origin = -> Origin283
  Type = Assembly
